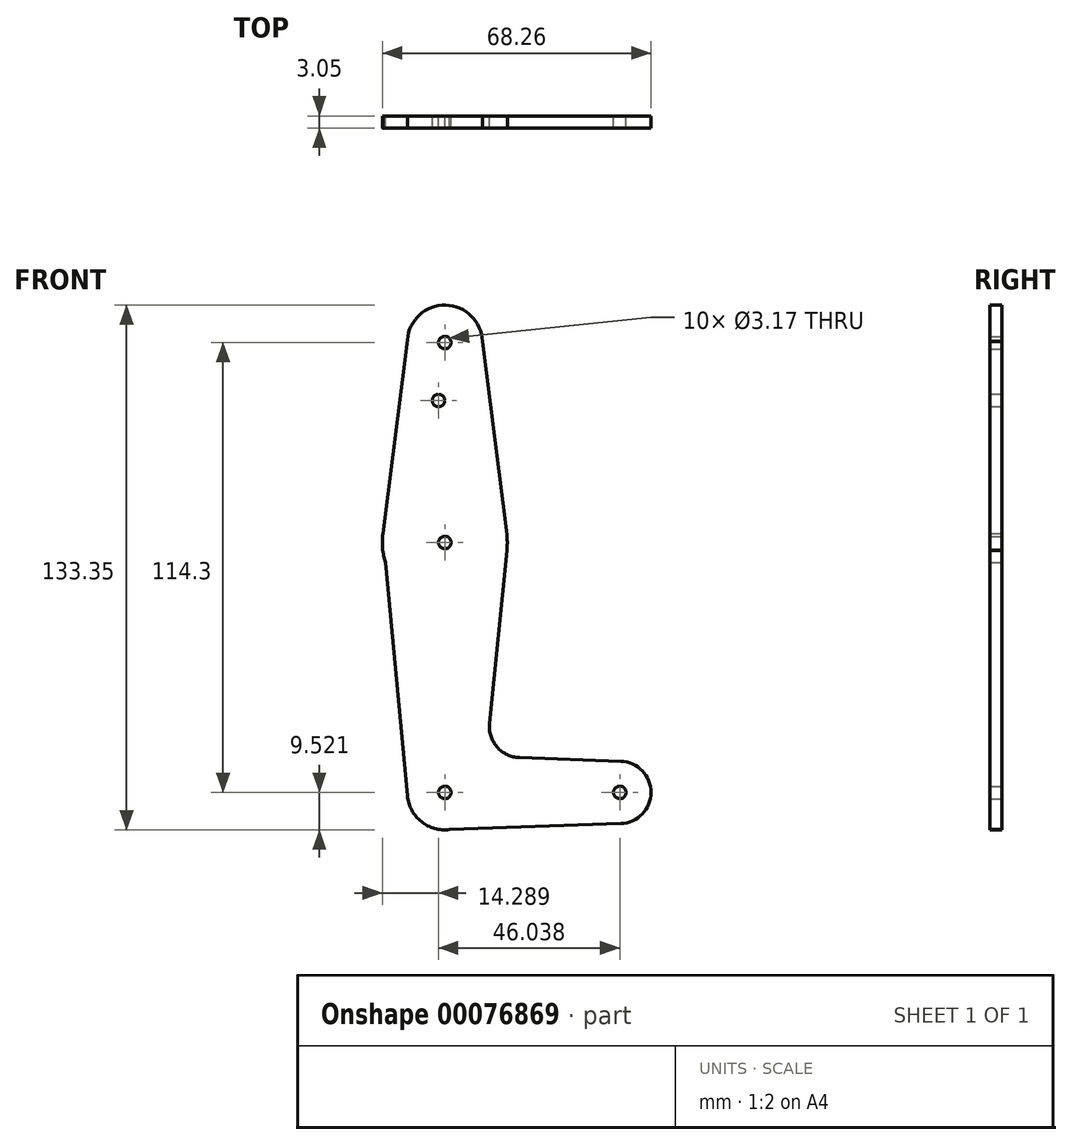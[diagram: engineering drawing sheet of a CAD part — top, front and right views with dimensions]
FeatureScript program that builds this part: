
annotation { "Feature Type Name" : "Feature", "Feature Type Description" : "" }
export const myFeature = defineFeature(function(context is Context, id is Id, definition is map)
    precondition{}
    {
        {
            var Q0;
            Q0=qCreatedBy(makeId("Front.planeOp"),FACE);
            var sketch = newSketch(context, id + "F0", { "sketchPlane" : qUnion([Q0])});
            skLineSegment(sketch, "E0", {"start": v(-30.74, 57.1) * mm, "end": v(-30.74, -57.2) * mm, "construction": true});
            skLineSegment(sketch, "E1", {"start": v(-30.74, -57.2) * mm, "end": v(13.7, -57.2) * mm, "construction": true});
            skCircle(sketch, "E2", {"center": v(-30.74, 57.1) * mm, "radius": 9.53 * mm});
            skCircle(sketch, "E3", {"center": v(13.7, -57.2) * mm, "radius": 7.94 * mm});
            skCircle(sketch, "E4", {"center": v(-30.74, -57.2) * mm, "radius": 9.53 * mm});
            skCircle(sketch, "E5", {"center": v(-30.74, 6.3) * mm, "radius": 15.88 * mm});
            skLineSegment(sketch, "E6", {"start": v(-40.25, 57.76) * mm, "end": v(-46.46, 8.56) * mm});
            skLineSegment(sketch, "E7", {"start": v(-46.46, 8.56) * mm, "end": v(-40.23, -58.09) * mm});
            skLineSegment(sketch, "E8", {"start": v(-11.78, -48.35) * mm, "end": v(13.99, -49.27) * mm});
            skCircle(sketch, "E9", {"center": v(-30.74, 6.3) * mm, "radius": 1.59 * mm});
            skCircle(sketch, "E10", {"center": v(-30.74, -57.2) * mm, "radius": 1.59 * mm});
            skCircle(sketch, "E11", {"center": v(13.7, -57.2) * mm, "radius": 1.59 * mm});
            skLineSegment(sketch, "E12", {"start": v(-21.22, 57.38) * mm, "end": v(-15, 8.3) * mm});
            skLineSegment(sketch, "E13", {"start": v(-15, 4.3) * mm, "end": v(-19.4, -39.6) * mm});
            skLineSegment(sketch, "E14", {"start": v(-29.57, -66.65) * mm, "end": v(13.98, -65.13) * mm});
            skCircle(sketch, "E15", {"center": v(-30.74, 57.1) * mm, "radius": 1.59 * mm});
            skArc(sketch, "E16.filletArc", {"start": v(-19.4, -39.6) * mm, "mid": v(-17.48, -45.63) * mm, "end": v(-11.78, -48.35) * mm});
            skCircle(sketch, "E17", {"center": v(-32.33, 42.37) * mm, "radius": 1.59 * mm});
            skSolve(sketch);
        }
        {
            var Q0;
            Q0 = qSketchRegion(id + "F0", true);
            extrude(context, id + "F1", {"entities" : qUnion([Q0]), "depth" : 3.05 * mm});
        }
        {
            var Q0;
            Q0 = qSketchRegion(id + "F0", true);
            extrude(context, id + "F2", {"entities" : qUnion([Q0]), "depth" : 3.05 * mm});
        }
    });
